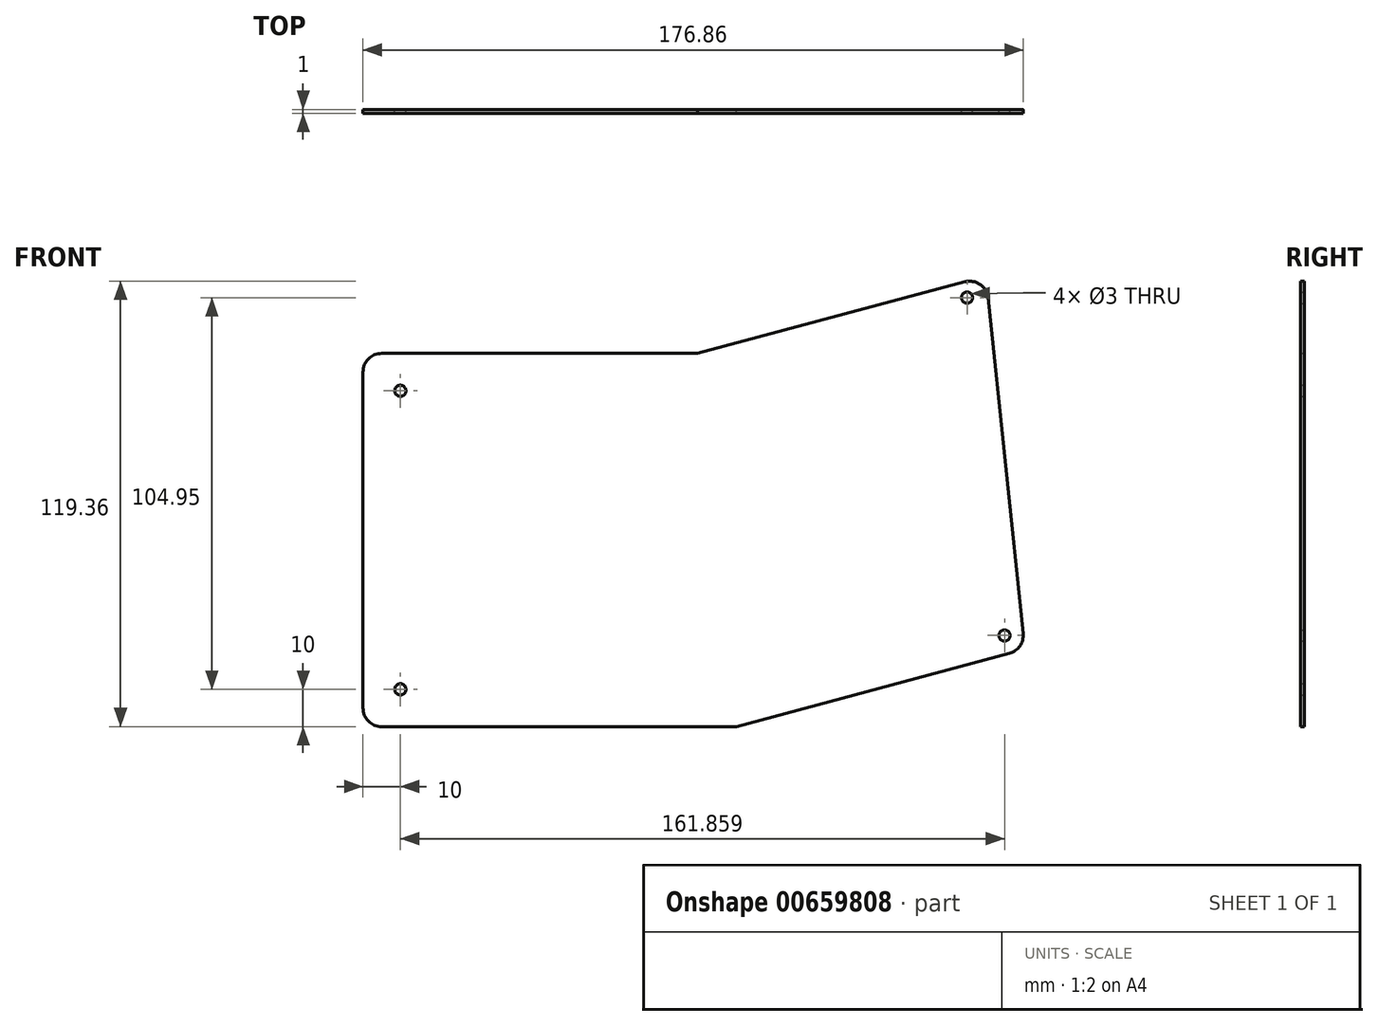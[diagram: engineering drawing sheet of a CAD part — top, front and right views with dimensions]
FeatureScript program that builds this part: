
annotation { "Feature Type Name" : "Feature", "Feature Type Description" : "" }
export const myFeature = defineFeature(function(context is Context, id is Id, definition is map)
    precondition{}
    {
        {
            var Q0;
            Q0=qCreatedBy(makeId("Front.planeOp"),FACE);
            var sketch = newSketch(context, id + "F0", { "sketchPlane" : qUnion([Q0])});
            skLineSegment(sketch, "E0", {"start": v(0, 5) * mm, "end": v(0, 95) * mm});
            skLineSegment(sketch, "E1", {"start": v(5, 100) * mm, "end": v(89.58, 100) * mm});
            skLineSegment(sketch, "E2", {"start": v(100, 0) * mm, "end": v(5, 0) * mm});
            skLineSegment(sketch, "E3", {"start": v(89.58, 100) * mm, "end": v(161.2, 119.19) * mm});
            skLineSegment(sketch, "E4", {"start": v(100, 0) * mm, "end": v(173.15, 19.6) * mm});
            skLineSegment(sketch, "E5", {"start": v(167.46, 114.88) * mm, "end": v(176.83, 24.95) * mm});
            skCircle(sketch, "E6", {"center": v(10, 90) * mm, "radius": 1.5 * mm});
            skCircle(sketch, "E7", {"center": v(10, 10) * mm, "radius": 1.5 * mm});
            skCircle(sketch, "E8", {"center": v(161.82, 114.95) * mm, "radius": 1.5 * mm});
            skCircle(sketch, "E9", {"center": v(171.86, 24.43) * mm, "radius": 1.5 * mm});
            skPoint(sketch, "E10.visualSharp", {"position": v(0, 100) * mm});
            skArc(sketch, "E10.filletArc", {"start": v(5, 100) * mm, "mid": v(1.46, 98.54) * mm, "end": v(0, 95) * mm});
            skPoint(sketch, "E11.visualSharp", {"position": v(0, 0) * mm});
            skArc(sketch, "E11.filletArc", {"start": v(0, 5) * mm, "mid": v(1.46, 1.46) * mm, "end": v(5, 0) * mm});
            skPoint(sketch, "E12.visualSharp", {"position": v(166.85, 120.7) * mm});
            skArc(sketch, "E12.filletArc", {"start": v(167.46, 114.88) * mm, "mid": v(165.32, 118.48) * mm, "end": v(161.2, 119.19) * mm});
            skPoint(sketch, "E13.visualSharp", {"position": v(177.27, 20.7) * mm});
            skArc(sketch, "E13.filletArc", {"start": v(173.15, 19.6) * mm, "mid": v(175.98, 21.6) * mm, "end": v(176.83, 24.95) * mm});
            skSolve(sketch);
        }
        {
            var Q0;
            Q0=makeQuery(id+"F0.imprint","IMPRINT",FACE,{"disambiguationData":[TD([[makeQuery(id+"F0.imprint","IMPRINT",EDGE,{"derivedFrom":sQuery(id+"F0.wireOp",EDGE,"E0")}),-1.0]])]});
            extrude(context, id + "F1", {"entities" : qUnion([Q0]), "depth" : 1 * mm, "offsetDistance" : 25 * mm});
        }
    });
